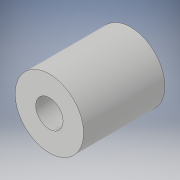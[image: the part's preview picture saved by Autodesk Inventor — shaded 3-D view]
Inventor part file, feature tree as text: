
AUTODESK INVENTOR PART (.ipt)
format: ipt  version: 2019 (Build 230136000, 136)  size: 132,608 bytes
history: native  units: mm
features: extrude x4, sketch x4, plane x1
ambient origin geometry x8: Origin, YZ Plane, XZ Plane, XY Plane, X Axis, Y Axis, Z Axis, Center Point
bodies: Solid1 (feature_tree)
feature tree (9):
  extrude  "Extrusion1"  Depth=6.0mm
  plane  "Work Plane1"
  extrude  "Extrusion2"  Depth=5.0mm
  extrude  "Extrusion3"  Depth=2.2mm
  extrude  "Extrusion4"  Depth=10.0mm TaperAngle=0.0deg
  sketch  "Sketch1"  dims[d0=15.0mm d1=6.0mm]
  sketch  "Sketch2"  dims[d2=17.8mm d3=0.0mm d4=5.0mm]
  sketch  "Sketch4"  dims[d5=5.5mm d6=2.2mm]
  sketch  "Sketch5"  dims[d7=5.2mm d8=10.0mm d9=0.0mm d12=3.0mm d13=4.0mm d14=8.0mm d15=0.0mm d16=6.0mm d17=7.0mm d18=0.5mm d19=8.0mm d20=0.0mm]
